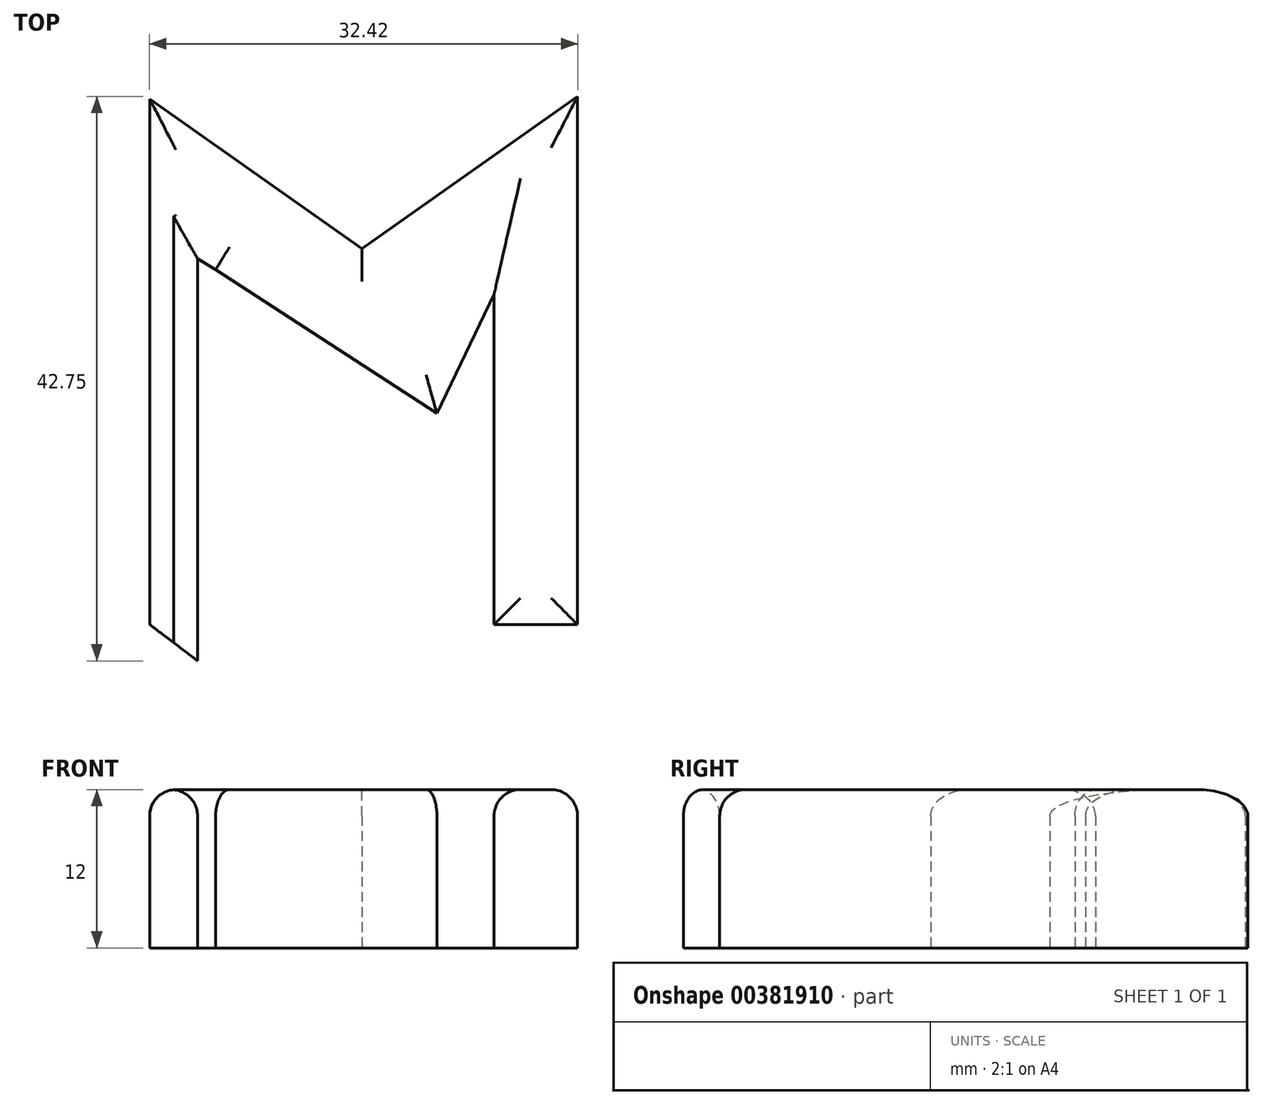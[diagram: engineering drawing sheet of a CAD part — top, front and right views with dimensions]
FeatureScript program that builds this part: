
annotation { "Feature Type Name" : "Feature", "Feature Type Description" : "" }
export const myFeature = defineFeature(function(context is Context, id is Id, definition is map)
    precondition{}
    {
        {
            var Q0;
            Q0=qCreatedBy(makeId("Top.planeOp"),FACE);
            var sketch = newSketch(context, id + "F0", { "sketchPlane" : qUnion([Q0])});
            skLineSegment(sketch, "E0", {"start": v(-99.84, -38.58) * mm, "end": v(-99.84, -78.58) * mm});
            skLineSegment(sketch, "E1", {"start": v(-100.1, -38.58) * mm, "end": v(-83.76, -50.11) * mm});
            skLineSegment(sketch, "E2", {"start": v(-83.76, -50.11) * mm, "end": v(-67.42, -38.58) * mm});
            skLineSegment(sketch, "E3", {"start": v(-67.42, -38.58) * mm, "end": v(-67.42, -78.58) * mm});
            skLineSegment(sketch, "E4", {"start": v(-96.2, -41.33) * mm, "end": v(-96.2, -81.33) * mm});
            skLineSegment(sketch, "E5", {"start": v(-94.83, -51.68) * mm, "end": v(-78.08, -62.6) * mm});
            skLineSegment(sketch, "E6", {"start": v(-78.08, -62.6) * mm, "end": v(-73.75, -53.58) * mm});
            skLineSegment(sketch, "E7", {"start": v(-73.75, -53.58) * mm, "end": v(-73.75, -63.58) * mm});
            skLineSegment(sketch, "E8", {"start": v(-73.75, -63.58) * mm, "end": v(-73.75, -73.58) * mm});
            skLineSegment(sketch, "E9", {"start": v(-73.75, -73.58) * mm, "end": v(-73.75, -78.58) * mm});
            skLineSegment(sketch, "E10", {"start": v(-73.75, -53.58) * mm, "end": v(-67.42, -38.58) * mm});
            skLineSegment(sketch, "E11", {"start": v(-94.83, -51.68) * mm, "end": v(-96.2, -50.86) * mm});
            skLineSegment(sketch, "E12", {"start": v(-99.84, -78.58) * mm, "end": v(-96.2, -81.33) * mm});
            skLineSegment(sketch, "E13", {"start": v(-73.75, -78.58) * mm, "end": v(-67.42, -78.58) * mm});
            skSolve(sketch);
        }
        {
            var Q0;
            Q0 = qSketchRegion(id + "F0", true);
            extrude(context, id + "F1", {"entities" : qUnion([Q0]), "depth" : 12 * mm});
        }
        {
            var Q0;
            Q0=makeQuery(id+"F1.opExtrude","CAP_EDGE",EDGE,{"disambiguationData":[OSD([sQuery(id+"F0.wireOp",EDGE,"E5")])],"isStart":false});
            var Q1;
            Q1=makeQuery(id+"F1.opExtrude","CAP_EDGE",EDGE,{"disambiguationData":[OSD([sQuery(id+"F0.wireOp",EDGE,"E2")])],"isStart":false});
            var Q2;
            Q2=makeQuery(id+"F1.opExtrude","CAP_EDGE",EDGE,{"disambiguationData":[OSD([sQuery(id+"F0.wireOp",EDGE,"E1")])],"isStart":false});
            var Q3;
            Q3=makeQuery(id+"F1.opExtrude","CAP_EDGE",EDGE,{"disambiguationData":[OSD([sQuery(id+"F0.wireOp",EDGE,"E4")])],"isStart":false});
            var Q4;
            Q4=makeQuery(id+"F1.opExtrude","CAP_EDGE",EDGE,{"disambiguationData":[OSD([sQuery(id+"F0.wireOp",EDGE,"E0")])],"isStart":false});
            var Q5;
            Q5=makeQuery(id+"F1.opExtrude","CAP_EDGE",EDGE,{"disambiguationData":[OSD([sQuery(id+"F0.wireOp",EDGE,"E6")])],"isStart":false});
            var Q6;
            Q6=makeQuery(id+"F1.opExtrude","CAP_EDGE",EDGE,{"disambiguationData":[OSD([sQuery(id+"F0.wireOp",EDGE,"E3")])],"isStart":false});
            var Q7;
            Q7=makeQuery(id+"F1.opExtrude","CAP_EDGE",EDGE,{"disambiguationData":[OSD([sQuery(id+"F0.wireOp",EDGE,"E7"),sQuery(id+"F0.wireOp",EDGE,"E8"),sQuery(id+"F0.wireOp",EDGE,"E9")])],"isStart":false});
            var Q8;
            Q8=makeQuery(id+"F1.opExtrude","CAP_EDGE",EDGE,{"disambiguationData":[OSD([sQuery(id+"F0.wireOp",EDGE,"E13")])],"isStart":false});
            fillet(context, id + "F2", {"entities" : qUnion([Q0, Q1, Q2, Q3, Q4, Q5, Q6, Q7, Q8]), "radius" : 2 * mm, "tangentPropagation" : true, "allowEdgeOverflow" : false});
        }
    });
